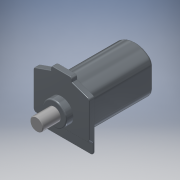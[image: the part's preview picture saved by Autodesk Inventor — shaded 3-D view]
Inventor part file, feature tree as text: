
AUTODESK INVENTOR PART (.ipt)
format: ipt  version: 2017.1 (Build 211199000, 199)  size: 285,696 bytes
history: native  units: mm
features: fillet x8, extrude x7, sketch x6, chamfer x2
ambient origin geometry x8: Origin, YZ Plane, XZ Plane, XY Plane, X Axis, Y Axis, Z Axis, Center Point
bodies: Solid1 (feature_tree)
feature tree (23):
  extrude  "Extrusion1"  Depth=55.3mm TaperAngle=0.0deg
  sketch  "Sketch2"  dims[d4=53.2mm d5=11.0mm d6=55.3mm d7=0.0mm d8=2.0mm]
  extrude  "Extrusion2"  Depth=2.0mm
  fillet  "Fillet2"  Radius=55.3mm
  fillet  "Fillet1"  Radius=2.0mm
  extrude  "Extrusion3"  Depth=12.9mm
  fillet  "Fillet3"  Radius=6.4mm
  extrude  "Extrusion4"  Depth=2.0mm
  extrude  "Extrusion5"  Depth=1.5mm TaperAngle=0.0deg
  chamfer  "Chamfer1"  Distance=4.5mm
  fillet  "Fillet4"  Radius=2.0mm
  fillet  "Fillet5"  Radius=2.0mm
  fillet  "Fillet6"  Radius=0.5mm
  fillet  "Fillet7"  Radius=45.0mm
  extrude  "Extrusion6"  Depth=2.0mm
  extrude  "Extrusion7"  Depth=2.0mm
  fillet  "Fillet8"  Radius=19.3mm
  chamfer  "Chamfer2"  Distance=5.7mm
  sketch  "Sketch1"  dims[d0=36.0mm d1=55.3mm d2=0.0mm]
  sketch  "Sketch3"  dims[d9=8.0mm d10=12.9mm d11=6.4mm d12=0.0mm]
  sketch  "Sketch4"  dims[d13=0.9mm d15=2.0mm]
  sketch  "Sketch5"  dims[d16=2.0mm d17=1.5mm d18=0.0mm d19=4.5mm d20=0.0mm]
  sketch  "Sketch6"  dims[d21=3.0mm d22=2.0mm d23=45.0deg d24=2.0mm d25=2.0mm d26=0.5mm d28=45.0mm d29=17.0mm d30=2.0mm d31=19.3mm d32=5.7mm d33=0.0mm d34=10.5mm d35=14.3mm d36=0.0mm d37=1.0mm d38=0.5mm d39=2.0mm d40=45.0deg]
